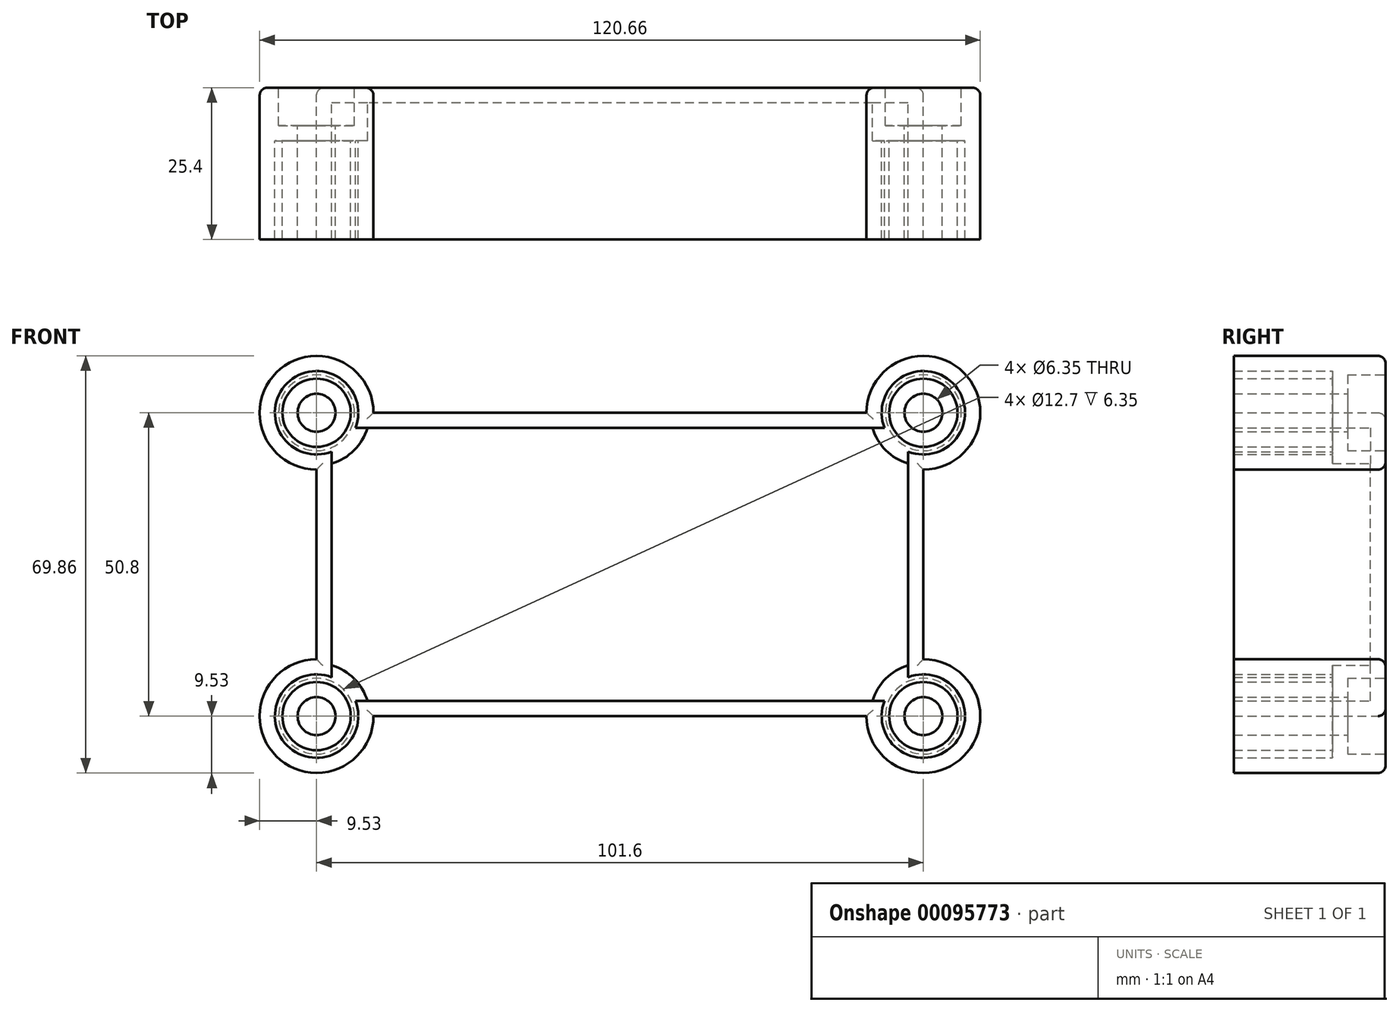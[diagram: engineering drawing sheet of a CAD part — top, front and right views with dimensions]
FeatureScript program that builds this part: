
annotation { "Feature Type Name" : "Feature", "Feature Type Description" : "" }
export const myFeature = defineFeature(function(context is Context, id is Id, definition is map)
    precondition{}
    {
        {
            var Q0;
            Q0=qCreatedBy(makeId("Front.planeOp"),FACE);
            var sketch = newSketch(context, id + "F0", { "sketchPlane" : qUnion([Q0])});
            skLineSegment(sketch, "E0.bottom", {"start": v(50.8, -25.4) * mm, "end": v(-50.8, -25.4) * mm});
            skLineSegment(sketch, "E0.top", {"start": v(50.8, 25.4) * mm, "end": v(-50.8, 25.4) * mm});
            skLineSegment(sketch, "E0.left", {"start": v(50.8, -25.4) * mm, "end": v(50.8, 25.4) * mm});
            skLineSegment(sketch, "E0.right", {"start": v(-50.8, -25.4) * mm, "end": v(-50.8, 25.4) * mm});
            skPoint(sketch, "E0.middle", {"position": v(0, 0) * mm});
            skArc(sketch, "E1", {"start": v(50.8, 15.88) * mm, "mid": v(57.54, 32.14) * mm, "end": v(41.28, 25.4) * mm});
            skArc(sketch, "E2", {"start": v(41.28, -25.4) * mm, "mid": v(57.54, -32.14) * mm, "end": v(50.8, -15.88) * mm});
            skArc(sketch, "E3", {"start": v(-41.28, 25.4) * mm, "mid": v(-57.54, 32.14) * mm, "end": v(-50.8, 15.88) * mm});
            skArc(sketch, "E4", {"start": v(-50.8, -15.88) * mm, "mid": v(-57.54, -32.14) * mm, "end": v(-41.28, -25.4) * mm});
            skSolve(sketch);
        }
        {
            var Q0;
            Q0 = qSketchRegion(id + "F0", true);
            extrude(context, id + "F1", {"entities" : qUnion([Q0]), "depth" : 25.4 * mm});
        }
        {
            var Q0;
            Q0=sQuery(id+"F0.wireOp",VERTEX,"E0.right.end");
            var Q1;
            Q1=sQuery(id+"F0.wireOp",VERTEX,"E0.bottom.start");
            var Q2;
            Q2=sQuery(id+"F0.wireOp",VERTEX,"E1.center");
            var Q3;
            Q3=sQuery(id+"F0.wireOp",VERTEX,"E0.right.start");
            var Q4;
            Q4=makeQuery(id+"F1.opExtrude","SWEPT_BODY",BODY,{"disambiguationData":[OSD([sQuery(id+"F0.wireOp",EDGE,"E0.bottom"),sQuery(id+"F0.wireOp",EDGE,"E0.top"),sQuery(id+"F0.wireOp",EDGE,"E0.left"),sQuery(id+"F0.wireOp",EDGE,"E0.right"),sQuery(id+"F0.wireOp",EDGE,"E1"),sQuery(id+"F0.wireOp",EDGE,"E2"),sQuery(id+"F0.wireOp",EDGE,"E3"),sQuery(id+"F0.wireOp",EDGE,"E4")])]});
            hole(context, id + "F2", {"style" : HoleStyle.C_BORE, "endStyle" : HoleEndStyle.THROUGH, "oppositeDirection" : true, "holeDiameter" : 6.35 * mm, "cBoreDiameter" : 12.7 * mm, "cBoreDepth" : 6.35 * mm, "locations" : qUnion([Q0, Q1, Q2, Q3]), "scope" : qUnion([Q4]), "isTappedThrough" : true});
        }
        {
            var Q0;
            Q0=makeQuery(id+"F1.opExtrude","CAP_FACE",FACE,{"disambiguationData":[OSD([sQuery(id+"F0.wireOp",EDGE,"E0.bottom"),sQuery(id+"F0.wireOp",EDGE,"E0.top"),sQuery(id+"F0.wireOp",EDGE,"E0.left"),sQuery(id+"F0.wireOp",EDGE,"E0.right"),sQuery(id+"F0.wireOp",EDGE,"E1"),sQuery(id+"F0.wireOp",EDGE,"E2"),sQuery(id+"F0.wireOp",EDGE,"E3"),sQuery(id+"F0.wireOp",EDGE,"E4")])],"isStart":false});
            shell(context, id + "F3", {"entities" : qUnion([Q0]), "thickness" : 2.54 * mm});
        }
        {
            var Q0;
            Q0=makeQuery(id+"F1.opExtrude","CAP_EDGE",EDGE,{"disambiguationData":[OSD([sQuery(id+"F0.wireOp",EDGE,"E0.top")])],"isStart":true});
            var Q1;
            Q1=makeQuery(id+"F1.opExtrude","CAP_EDGE",EDGE,{"disambiguationData":[OSD([sQuery(id+"F0.wireOp",EDGE,"E0.right")])],"isStart":true});
            var Q2;
            Q2=makeQuery(id+"F1.opExtrude","CAP_EDGE",EDGE,{"disambiguationData":[OSD([sQuery(id+"F0.wireOp",EDGE,"E0.bottom")])],"isStart":true});
            var Q3;
            Q3=makeQuery(id+"F1.opExtrude","CAP_EDGE",EDGE,{"disambiguationData":[OSD([sQuery(id+"F0.wireOp",EDGE,"E0.left")])],"isStart":true});
            var Q4;
            Q4=makeQuery(id+"F1.opExtrude","CAP_EDGE",EDGE,{"disambiguationData":[OSD([sQuery(id+"F0.wireOp",EDGE,"E3")])],"isStart":true});
            var Q5;
            Q5=makeQuery(id+"F1.opExtrude","CAP_EDGE",EDGE,{"disambiguationData":[OSD([sQuery(id+"F0.wireOp",EDGE,"E1")])],"isStart":true});
            var Q6;
            Q6=makeQuery(id+"F1.opExtrude","CAP_EDGE",EDGE,{"disambiguationData":[OSD([sQuery(id+"F0.wireOp",EDGE,"E2")])],"isStart":true});
            var Q7;
            Q7=makeQuery(id+"F1.opExtrude","CAP_EDGE",EDGE,{"disambiguationData":[OSD([sQuery(id+"F0.wireOp",EDGE,"E4")])],"isStart":true});
            fillet(context, id + "F4", {"entities" : qUnion([Q0, Q1, Q2, Q3, Q4, Q5, Q6, Q7]), "radius" : 1.27 * mm, "tangentPropagation" : true, "allowEdgeOverflow" : false});
        }
    });
